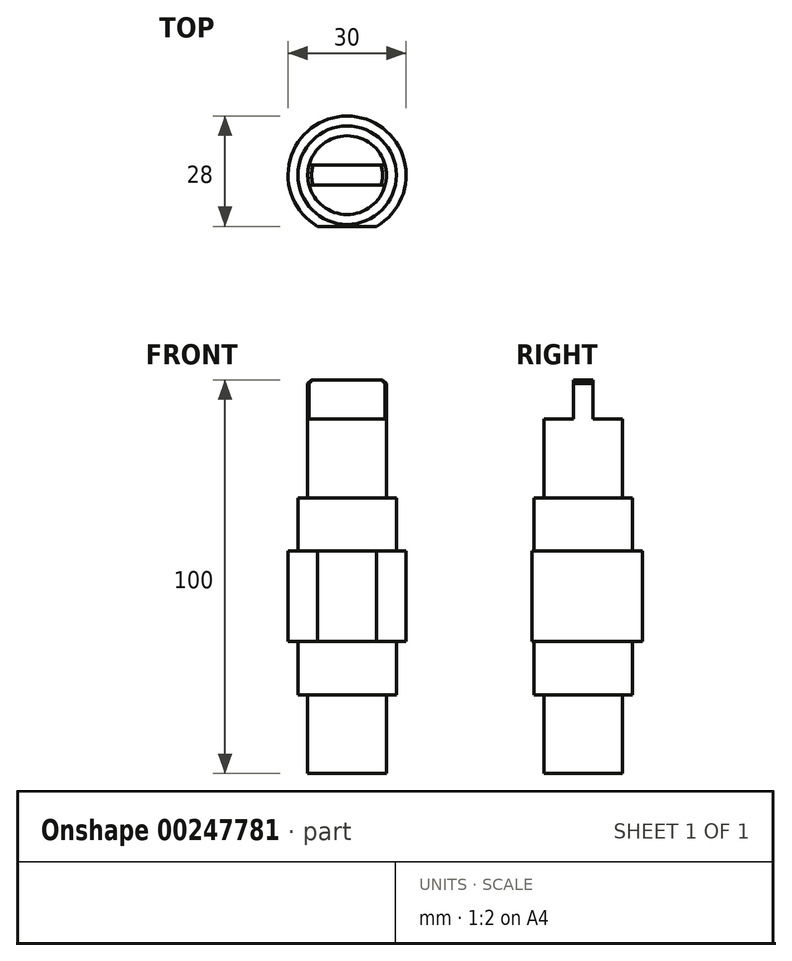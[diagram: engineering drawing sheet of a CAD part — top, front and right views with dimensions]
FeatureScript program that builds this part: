
annotation { "Feature Type Name" : "Feature", "Feature Type Description" : "" }
export const myFeature = defineFeature(function(context is Context, id is Id, definition is map)
    precondition{}
    {
        {
            var Q0;
            Q0=qCreatedBy(makeId("Front.planeOp"),FACE);
            var sketch = newSketch(context, id + "F0", { "sketchPlane" : qUnion([Q0])});
            skLineSegment(sketch, "E0", {"start": v(-15, 11.5) * mm, "end": v(-15, 0) * mm});
            skLineSegment(sketch, "E1", {"start": v(-10, 45) * mm, "end": v(0, 45) * mm});
            skLineSegment(sketch, "E2.MirrorCS", {"start": v(-15, 0) * mm, "end": v(-15, 11.5) * mm});
            skLineSegment(sketch, "E3", {"start": v(0, 45) * mm, "end": v(0, 0) * mm});
            skLineSegment(sketch, "E4", {"start": v(-15, 11.5) * mm, "end": v(-12.5, 11.5) * mm});
            skLineSegment(sketch, "E5", {"start": v(-12.5, 25) * mm, "end": v(-12.5, 11.5) * mm});
            skLineSegment(sketch, "E6", {"start": v(-12.5, 25) * mm, "end": v(-10, 25) * mm});
            skLineSegment(sketch, "E7", {"start": v(-10, 45) * mm, "end": v(-10, 25) * mm});
            skLineSegment(sketch, "E8", {"start": v(12.24, 0) * mm, "end": v(-26.8, 0) * mm, "construction": true});
            skLineSegment(sketch, "E9.MirrorCS", {"start": v(0, -45) * mm, "end": v(0, 0) * mm});
            skLineSegment(sketch, "E10.MirrorCS", {"start": v(-10, -45) * mm, "end": v(0, -45) * mm});
            skLineSegment(sketch, "E11.MirrorCS", {"start": v(-10, -45) * mm, "end": v(-10, -25) * mm});
            skLineSegment(sketch, "E12.MirrorCS", {"start": v(-12.5, -25) * mm, "end": v(-10, -25) * mm});
            skLineSegment(sketch, "E13.MirrorCS", {"start": v(-12.5, -25) * mm, "end": v(-12.5, -11.5) * mm});
            skLineSegment(sketch, "E14.MirrorCS", {"start": v(-15, -11.5) * mm, "end": v(-12.5, -11.5) * mm});
            skLineSegment(sketch, "E15.MirrorCS", {"start": v(-15, 0) * mm, "end": v(-15, -11.5) * mm});
            skSolve(sketch);
        }
        {
            var Q0;
            Q0=qSketchRegion(id+"F0",true);
            var Q1;
            Q1=sQuery(id+"F0.wireOp",EDGE,"E3");
            revolve(context, id + "F1", {"entities" : qUnion([Q0]), "axis" : qUnion([Q1]), "revolveType" : RevolveType.FULL});
        }
        {
            var Q0;
            Q0=qCreatedBy(makeId("Top.planeOp"),FACE);
            var sketch = newSketch(context, id + "F2", { "sketchPlane" : qUnion([Q0])});
            skLineSegment(sketch, "E16", {"start": v(-18, -12.5) * mm, "end": v(24.59, -12.5) * mm, "construction": true});
            skLineSegment(sketch, "E17", {"start": v(-15, -13) * mm, "end": v(0, -13) * mm});
            skLineSegment(sketch, "E18", {"start": v(-15, -17) * mm, "end": v(0, -17) * mm});
            skLineSegment(sketch, "E19.trimOffspring", {"start": v(-15, -13) * mm, "end": v(-15, -17) * mm});
            skLineSegment(sketch, "E20.MirrorCS", {"start": v(15, -13) * mm, "end": v(0, -13) * mm});
            skLineSegment(sketch, "E21.MirrorCS", {"start": v(15, -13) * mm, "end": v(15, -17) * mm});
            skLineSegment(sketch, "E22.MirrorCS", {"start": v(15, -17) * mm, "end": v(0, -17) * mm});
            skCircle(sketch, "E23.0", {"center": v(0, 0) * mm, "radius": 10 * mm, "construction": true});
            skCircle(sketch, "E24.0", {"center": v(0, 0) * mm, "radius": 12.5 * mm, "construction": true});
            skSolve(sketch);
        }
        {
            var Q0;
            Q0=qSketchRegion(id+"F2",true);
            extrude(context, id + "F3", {"entities" : qUnion([Q0]), "operationType" : NewBodyOperationType.REMOVE, "depth" : 25 * mm, "hasSecondDirection" : true, "secondDirectionOppositeDirection" : true, "secondDirectionDepth" : 25 * mm});
        }
        {
            var Q0;
            Q0=makeQuery(id+"F1.opRevolve","SWEPT_FACE",FACE,{"disambiguationData":[OSD([sQuery(id+"F0.wireOp",EDGE,"E1")])]});
            cPlane(context, id + "F4", {"entities" : qUnion([Q0]), "cplaneType" : CPlaneType.OFFSET, "offset" : 0 * mm, "width" : 150 * mm, "height" : 150 * mm});
        }
        {
            var Q0;
            Q0=qCreatedBy(id+"F4.planeOp",FACE);
            var sketch = newSketch(context, id + "F5", { "sketchPlane" : qUnion([Q0])});
            skArc(sketch, "E25.0.0", {"start": v(-9.68, 2.5) * mm, "mid": v(-10, 0) * mm, "end": v(-9.68, -2.5) * mm});
            skLineSegment(sketch, "E26", {"start": v(-9.68, 2.5) * mm, "end": v(9.68, 2.5) * mm});
            skLineSegment(sketch, "E27.MirrorCS", {"start": v(-9.68, -2.5) * mm, "end": v(9.68, -2.5) * mm});
            skArc(sketch, "E28.trimOffspring", {"start": v(9.68, -2.5) * mm, "mid": v(10, 0) * mm, "end": v(9.68, 2.5) * mm});
            skSolve(sketch);
        }
        {
            var Q0;
            Q0=qSketchRegion(id+"F5",true);
            extrude(context, id + "F6", {"entities" : qUnion([Q0]), "operationType" : NewBodyOperationType.ADD, "depth" : 10 * mm, "hasSecondDirection" : true, "secondDirectionOppositeDirection" : true, "secondDirectionDepth" : 10 * mm});
        }
        {
            var Q0;
            Q0=makeQuery(id+"F6.opExtrude","CAP_EDGE",EDGE,{"disambiguationData":[OSD([sQuery(id+"F5.wireOp",EDGE,"E28.trimOffspring")])],"isStart":false});
            var Q1;
            Q1=makeQuery(id+"F6.opExtrude","CAP_EDGE",EDGE,{"disambiguationData":[OSD([sQuery(id+"F5.wireOp",EDGE,"E25.0.0")])],"isStart":false});
            chamfer(context, id + "F7", {"entities" : qUnion([Q0, Q1]), "width" : 1 * mm, "tangentPropagation" : true});
        }
    });
